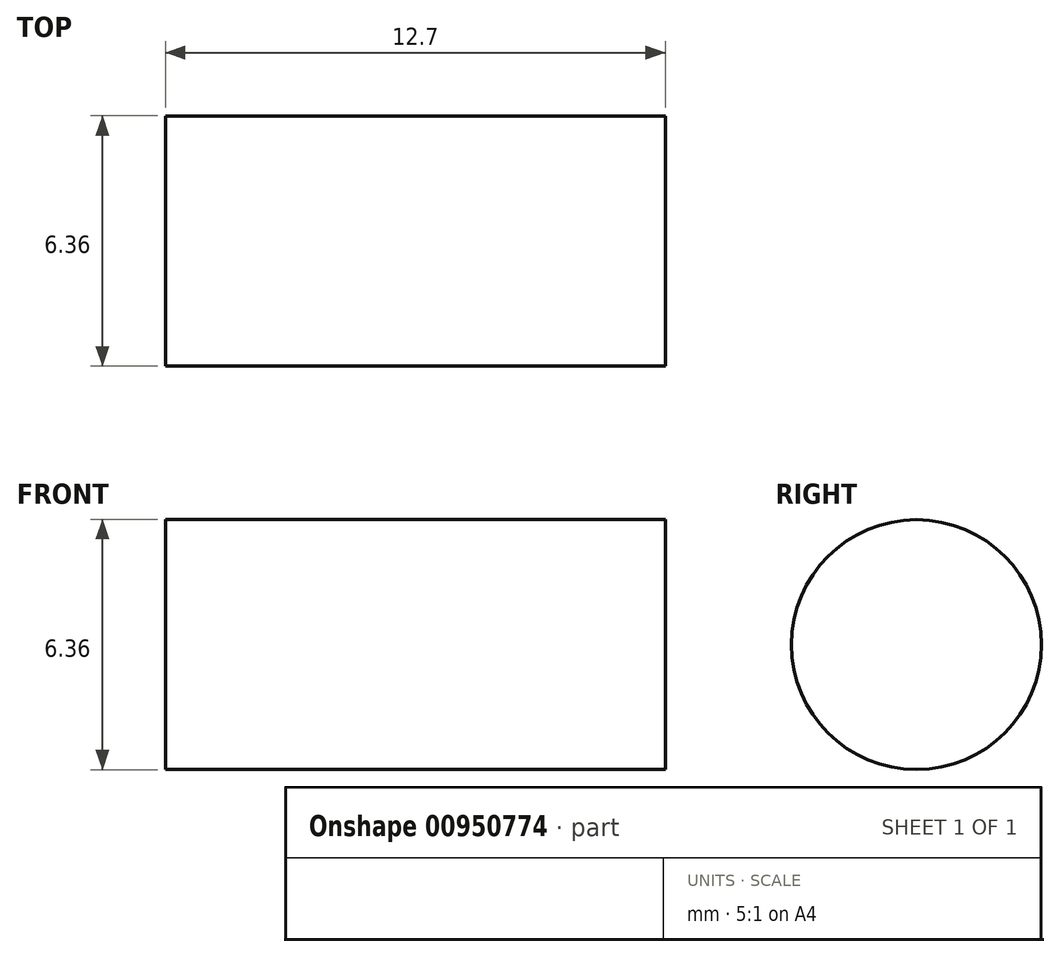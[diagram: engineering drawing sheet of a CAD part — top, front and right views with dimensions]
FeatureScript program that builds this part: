
annotation { "Feature Type Name" : "Feature", "Feature Type Description" : "" }
export const myFeature = defineFeature(function(context is Context, id is Id, definition is map)
    precondition{}
    {
        {
            var Q0;
            Q0=qCreatedBy(makeId("Right.planeOp"),FACE);
            var sketch = newSketch(context, id + "F0", { "sketchPlane" : qUnion([Q0])});
            skLineSegment(sketch, "E0", {"start": v(0, 0) * mm, "end": v(-3.18, 0) * mm});
            skCircle(sketch, "E1", {"center": v(0, 0) * mm, "radius": 3.18 * mm});
            skSolve(sketch);
        }
        {
            var Q0;
            Q0=makeQuery(id+"F0.imprint","IMPRINT",FACE,{"disambiguationData":[TD([[makeQuery(id+"F0.imprint","IMPRINT",EDGE,{"derivedFrom":sQuery(id+"F0.wireOp",EDGE,"E1")}),1.0]])]});
            extrude(context, id + "F1", {"entities" : qUnion([Q0]), "depth" : 12.7 * mm, "offsetDistance" : 25.4 * mm});
        }
    });
